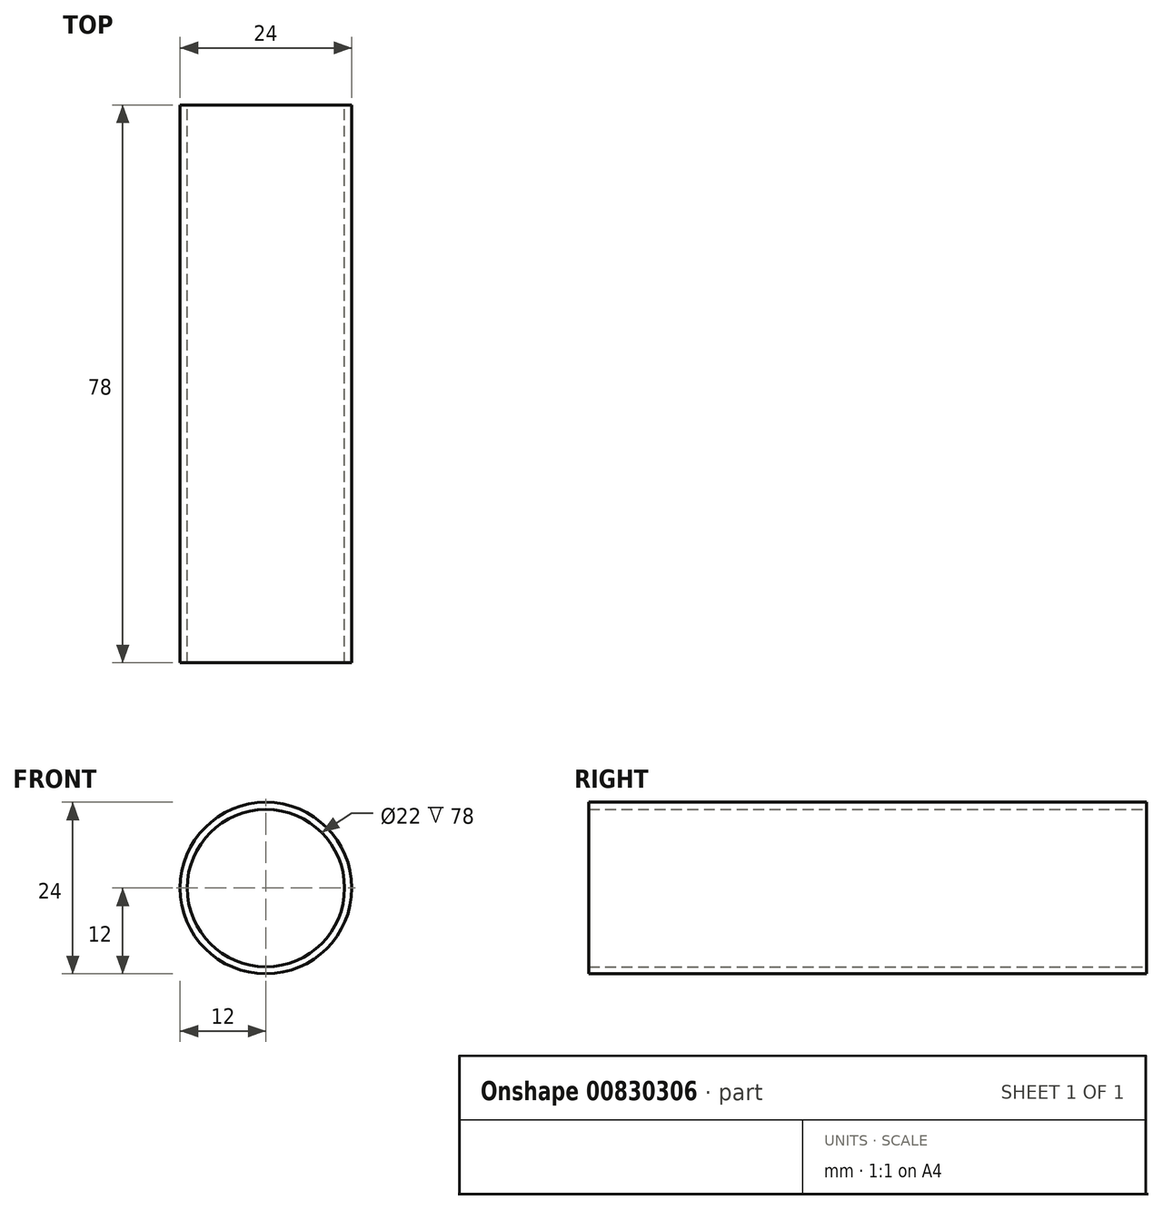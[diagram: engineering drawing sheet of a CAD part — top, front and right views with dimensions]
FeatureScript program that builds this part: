
annotation { "Feature Type Name" : "Feature", "Feature Type Description" : "" }
export const myFeature = defineFeature(function(context is Context, id is Id, definition is map)
    precondition{}
    {
        {
            var Q0;
            Q0=qCreatedBy(makeId("Front.planeOp"),FACE);
            var sketch = newSketch(context, id + "F0", { "sketchPlane" : qUnion([Q0])});
            skCircle(sketch, "E0", {"center": v(0, 0) * mm, "radius": 12 * mm});
            skCircle(sketch, "E1.0", {"center": v(0, 0) * mm, "radius": 11 * mm});
            skSolve(sketch);
        }
        {
            var Q0;
            Q0=makeQuery(id+"F0.imprint","IMPRINT",FACE,{"disambiguationData":[TD([[makeQuery(id+"F0.imprint","IMPRINT",EDGE,{"derivedFrom":sQuery(id+"F0.wireOp",EDGE,"E0")}),1.0]])]});
            extrude(context, id + "F1", {"entities" : qUnion([Q0]), "depth" : 78 * mm, "offsetDistance" : 25 * mm});
        }
    });
